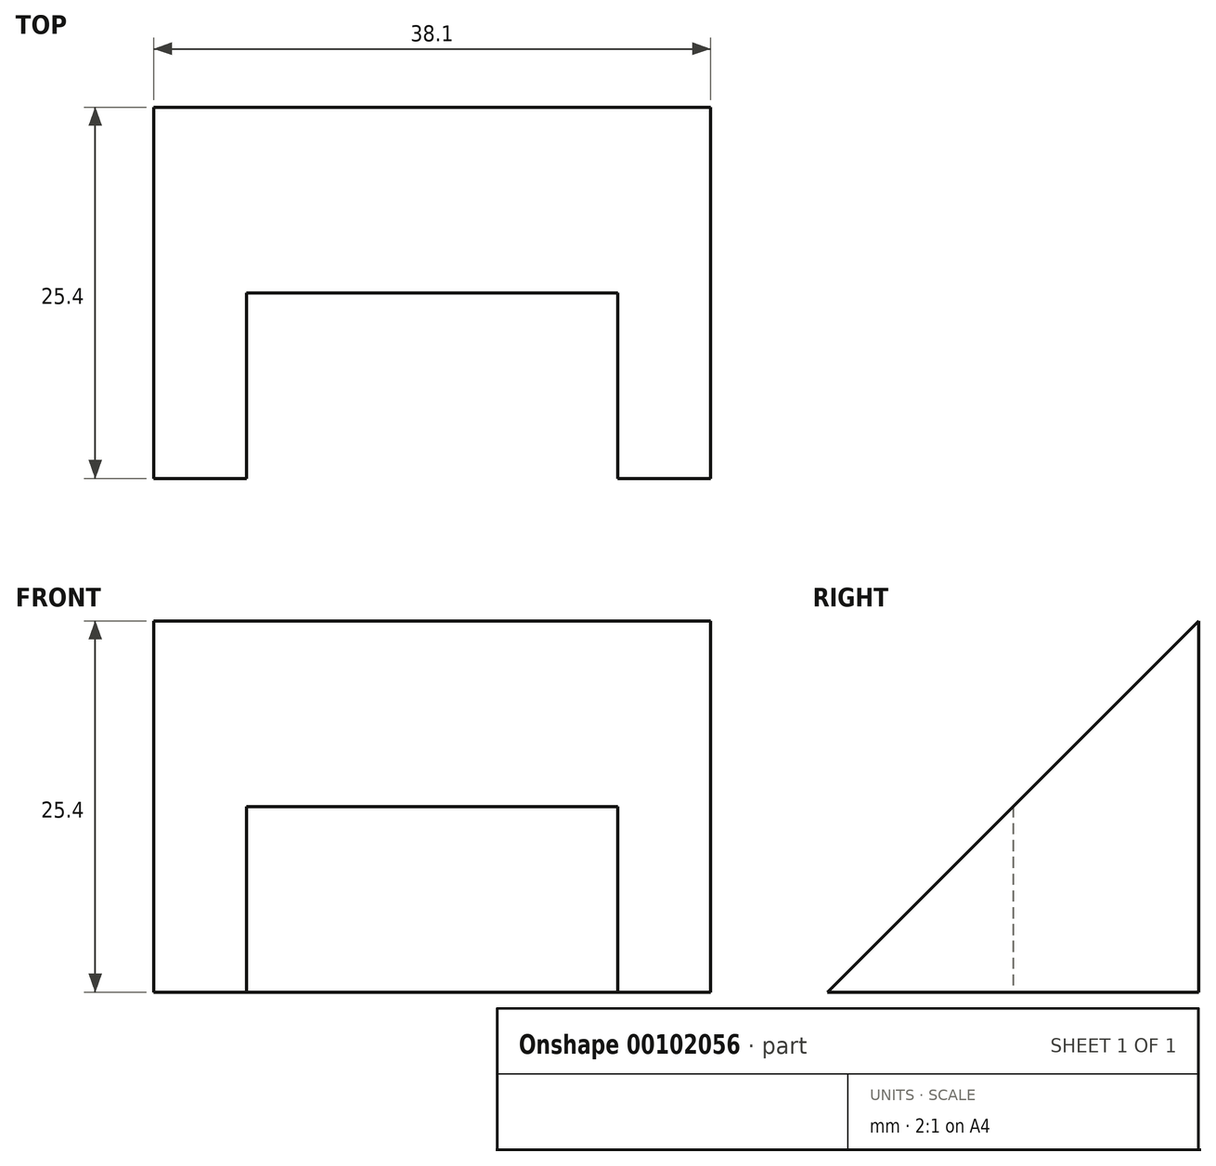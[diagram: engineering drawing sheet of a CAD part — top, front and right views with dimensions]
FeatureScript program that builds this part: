
annotation { "Feature Type Name" : "Feature", "Feature Type Description" : "" }
export const myFeature = defineFeature(function(context is Context, id is Id, definition is map)
    precondition{}
    {
        {
            var Q0;
            Q0=qCreatedBy(makeId("Right.planeOp"),FACE);
            var sketch = newSketch(context, id + "F0", { "sketchPlane" : qUnion([Q0])});
            skLineSegment(sketch, "E0", {"start": v(0, 0) * mm, "end": v(-25.4, 0) * mm});
            skLineSegment(sketch, "E1", {"start": v(-25.4, 0) * mm, "end": v(0, 25.4) * mm});
            skLineSegment(sketch, "E2", {"start": v(0, 25.4) * mm, "end": v(0, 0) * mm});
            skSolve(sketch);
        }
        {
            var Q0;
            Q0 = qSketchRegion(id + "F0", true);
            extrude(context, id + "F1", {"entities" : qUnion([Q0]), "depth" : 38.1 * mm});
        }
        {
            var Q0;
            Q0=qCreatedBy(makeId("Top.planeOp"),FACE);
            var sketch = newSketch(context, id + "F2", { "sketchPlane" : qUnion([Q0])});
            skLineSegment(sketch, "E3", {"start": v(6.35, -25.4) * mm, "end": v(6.35, -12.7) * mm});
            skLineSegment(sketch, "E4", {"start": v(6.35, -12.7) * mm, "end": v(31.75, -12.7) * mm});
            skLineSegment(sketch, "E5", {"start": v(31.75, -12.7) * mm, "end": v(31.75, -25.4) * mm});
            skLineSegment(sketch, "E6", {"start": v(31.75, -25.4) * mm, "end": v(6.35, -25.4) * mm});
            skSolve(sketch);
        }
        {
            var Q0;
            Q0 = qSketchRegion(id + "F2", true);
            extrude(context, id + "F3", {"entities" : qUnion([Q0]), "operationType" : NewBodyOperationType.REMOVE, "depth" : 25.4 * mm});
        }
    });
